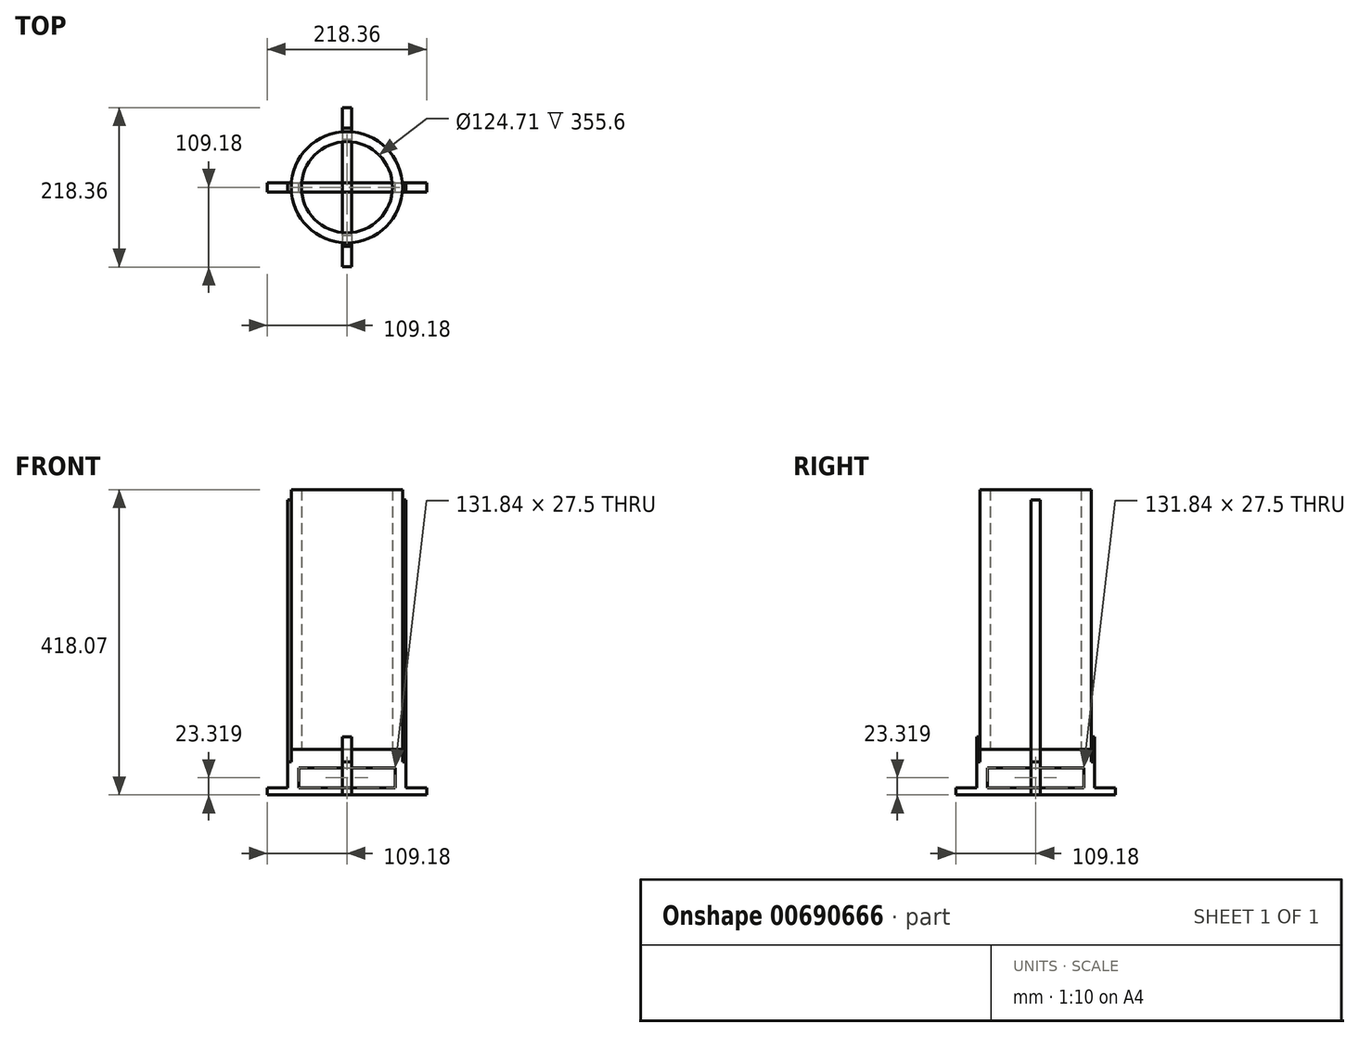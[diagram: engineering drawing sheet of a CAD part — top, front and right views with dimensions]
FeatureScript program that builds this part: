
annotation { "Feature Type Name" : "Feature", "Feature Type Description" : "" }
export const myFeature = defineFeature(function(context is Context, id is Id, definition is map)
    precondition{}
    {
        {
            var Q0;
            Q0=qCreatedBy(makeId("Top.planeOp"),FACE);
            var sketch = newSketch(context, id + "F0", { "sketchPlane" : qUnion([Q0])});
            skCircle(sketch, "E0", {"center": v(0, 0) * mm, "radius": 76.2 * mm});
            skCircle(sketch, "E1.0", {"center": v(0, 0) * mm, "radius": 62.36 * mm});
            skSolve(sketch);
        }
        {
            var Q0;
            Q0 = qSketchRegion(id + "F0", true);
            extrude(context, id + "F1", {"entities" : qUnion([Q0]), "depth" : 355.6 * mm, "offsetDistance" : 25.4 * mm});
        }
        {
            var Q0;
            Q0=qCreatedBy(makeId("Front.planeOp"),FACE);
            var sketch = newSketch(context, id + "F2", { "sketchPlane" : qUnion([Q0])});
            skLineSegment(sketch, "E2", {"start": v(0, 0) * mm, "end": v(76.2, 0) * mm});
            skLineSegment(sketch, "E3", {"start": v(65.92, -52.9) * mm, "end": v(65.92, -25.4) * mm});
            skLineSegment(sketch, "E4", {"start": v(65.92, -25.4) * mm, "end": v(0, -25.4) * mm});
            skLineSegment(sketch, "E5", {"start": v(76.2, 0) * mm, "end": v(76.2, -16.95) * mm});
            skLineSegment(sketch, "E6", {"start": v(76.2, -16.95) * mm, "end": v(80.84, -16.95) * mm});
            skLineSegment(sketch, "E7", {"start": v(80.84, -16.95) * mm, "end": v(80.84, -52.9) * mm});
            skLineSegment(sketch, "E8", {"start": v(0, 0) * mm, "end": v(0, -25.4) * mm});
            skLineSegment(sketch, "E9", {"start": v(80.84, -52.9) * mm, "end": v(65.92, -52.9) * mm});
            skLineSegment(sketch, "E10.bottom", {"start": v(0, -52.9) * mm, "end": v(0, -52.9) * mm});
            skLineSegment(sketch, "E10.left", {"start": v(0, -52.9) * mm, "end": v(0, -62.47) * mm});
            skLineSegment(sketch, "E10.right", {"start": v(0, -52.9) * mm, "end": v(0, -62.47) * mm});
            skLineSegment(sketch, "E11.bottom", {"start": v(0, -52.9) * mm, "end": v(109.18, -52.9) * mm});
            skLineSegment(sketch, "E11.top", {"start": v(0, -62.47) * mm, "end": v(109.18, -62.47) * mm});
            skLineSegment(sketch, "E11.right", {"start": v(109.18, -52.9) * mm, "end": v(109.18, -62.47) * mm});
            skLineSegment(sketch, "E12.MirrorCS", {"start": v(-76.2, -16.95) * mm, "end": v(-80.84, -16.95) * mm});
            skLineSegment(sketch, "E13.MirrorCS", {"start": v(-76.2, 0) * mm, "end": v(-76.2, -16.95) * mm});
            skLineSegment(sketch, "E14.MirrorCS", {"start": v(-80.84, -52.9) * mm, "end": v(-65.92, -52.9) * mm});
            skLineSegment(sketch, "E15.MirrorCS", {"start": v(-109.18, -52.9) * mm, "end": v(-109.18, -62.47) * mm});
            skLineSegment(sketch, "E16.MirrorCS", {"start": v(-65.92, -25.4) * mm, "end": v(0, -25.4) * mm});
            skLineSegment(sketch, "E17.MirrorCS", {"start": v(0, -52.9) * mm, "end": v(-109.18, -52.9) * mm});
            skLineSegment(sketch, "E18.MirrorCS", {"start": v(0, -62.47) * mm, "end": v(-109.18, -62.47) * mm});
            skLineSegment(sketch, "E19.MirrorCS", {"start": v(-65.92, -52.9) * mm, "end": v(-65.92, -25.4) * mm});
            skLineSegment(sketch, "E20.MirrorCS", {"start": v(0, 0) * mm, "end": v(-76.2, 0) * mm});
            skLineSegment(sketch, "E21.MirrorCS", {"start": v(-80.84, -16.95) * mm, "end": v(-80.84, -52.9) * mm});
            skSolve(sketch);
        }
        {
            var Q0;
            Q0 = qSketchRegion(id + "F2", true);
            extrude(context, id + "F3", {"entities" : qUnion([Q0]), "endBound" : BoundingType.SYMMETRIC, "depth" : 12.7 * mm, "offsetDistance" : 25.4 * mm});
        }
        {
            var Q0;
            Q0=makeQuery(id+"F3.opExtrude","SWEPT_BODY",BODY,{"disambiguationData":[OSD([sQuery(id+"F2.wireOp",EDGE,"E2"),sQuery(id+"F2.wireOp",EDGE,"E3"),sQuery(id+"F2.wireOp",EDGE,"E4"),sQuery(id+"F2.wireOp",EDGE,"E5"),sQuery(id+"F2.wireOp",EDGE,"E6"),sQuery(id+"F2.wireOp",EDGE,"E7"),sQuery(id+"F2.wireOp",EDGE,"yYa1QQtk-rfeQ-uA0k-yN95-LENgFDuBBmhA"),sQuery(id+"F2.wireOp",EDGE,"RaL1Y38n-DL0R-HpUy-0Yu0-hKOuieMtGCDP"),sQuery(id+"F2.wireOp",EDGE,"KzeCX9vK-PA9l-fBDc-L8z4-hnWVkcK37siH"),sQuery(id+"F2.wireOp",EDGE,"7a3115bd-42c9-43fa-886f-b7d7f014f3800.MirrorCS"),sQuery(id+"F2.wireOp",EDGE,"93714e8b-1b55-43fa-9f0a-1818bfe9d4330.MirrorCS"),sQuery(id+"F2.wireOp",EDGE,"f685ec73-5cd7-40c9-a0cc-09a82770efb00.MirrorCS"),sQuery(id+"F2.wireOp",EDGE,"605de593-ab4b-4a38-8b95-8d2e6ad95e7e0.MirrorCS"),sQuery(id+"F2.wireOp",EDGE,"bd68596d-ea5b-43b6-8ec0-eaa4091035650.MirrorCS"),sQuery(id+"F2.wireOp",EDGE,"6dadb6d6-938b-41b2-89eb-21b29489f2620.MirrorCS"),sQuery(id+"F2.wireOp",EDGE,"35a6b2d6-89f1-42be-bee9-e52b24f0a85c0.MirrorCS"),sQuery(id+"F2.wireOp",EDGE,"99d46e2b-beb4-45a8-a67b-b38dd53197940.MirrorCS"),sQuery(id+"F2.wireOp",EDGE,"687b68df-4fec-4741-9a90-ace4315f9af80.MirrorCS")])]});
            transform(context, id + "F4", {"entities" : qUnion([Q0]), "transformType" : TransformType.COPY});
        }
        {
            var Q0;
            Q0=makeQuery(id+"F3.opExtrude","SWEPT_BODY",BODY,{"disambiguationData":[OSD([sQuery(id+"F2.wireOp",EDGE,"E2"),sQuery(id+"F2.wireOp",EDGE,"E3"),sQuery(id+"F2.wireOp",EDGE,"E4"),sQuery(id+"F2.wireOp",EDGE,"E5"),sQuery(id+"F2.wireOp",EDGE,"E6"),sQuery(id+"F2.wireOp",EDGE,"E7"),sQuery(id+"F2.wireOp",EDGE,"yYa1QQtk-rfeQ-uA0k-yN95-LENgFDuBBmhA"),sQuery(id+"F2.wireOp",EDGE,"RaL1Y38n-DL0R-HpUy-0Yu0-hKOuieMtGCDP"),sQuery(id+"F2.wireOp",EDGE,"KzeCX9vK-PA9l-fBDc-L8z4-hnWVkcK37siH"),sQuery(id+"F2.wireOp",EDGE,"7a3115bd-42c9-43fa-886f-b7d7f014f3800.MirrorCS"),sQuery(id+"F2.wireOp",EDGE,"93714e8b-1b55-43fa-9f0a-1818bfe9d4330.MirrorCS"),sQuery(id+"F2.wireOp",EDGE,"f685ec73-5cd7-40c9-a0cc-09a82770efb00.MirrorCS"),sQuery(id+"F2.wireOp",EDGE,"605de593-ab4b-4a38-8b95-8d2e6ad95e7e0.MirrorCS"),sQuery(id+"F2.wireOp",EDGE,"bd68596d-ea5b-43b6-8ec0-eaa4091035650.MirrorCS"),sQuery(id+"F2.wireOp",EDGE,"6dadb6d6-938b-41b2-89eb-21b29489f2620.MirrorCS"),sQuery(id+"F2.wireOp",EDGE,"35a6b2d6-89f1-42be-bee9-e52b24f0a85c0.MirrorCS"),sQuery(id+"F2.wireOp",EDGE,"99d46e2b-beb4-45a8-a67b-b38dd53197940.MirrorCS"),sQuery(id+"F2.wireOp",EDGE,"687b68df-4fec-4741-9a90-ace4315f9af80.MirrorCS")])]});
            var Q1;
            Q1=sQuery(id+"F2.wireOp",EDGE,"E8");
            transform(context, id + "F5", {"entities" : qUnion([Q0]), "transformType" : TransformType.ROTATION, "transformAxis" : qUnion([Q1]), "angle" : 90 * degree, "makeCopy" : false});
        }
        {
            var Q0;
            Q0=makeQuery(id+"F4.opPattern","COPY",FACE,{"derivedFrom":makeQuery(id+"F3.opExtrude","CAP_FACE",FACE,{"disambiguationData":[OSD([sQuery(id+"F2.wireOp",EDGE,"E2"),sQuery(id+"F2.wireOp",EDGE,"E3"),sQuery(id+"F2.wireOp",EDGE,"E4"),sQuery(id+"F2.wireOp",EDGE,"E5"),sQuery(id+"F2.wireOp",EDGE,"E6"),sQuery(id+"F2.wireOp",EDGE,"E7"),sQuery(id+"F2.wireOp",EDGE,"E11.bottom"),sQuery(id+"F2.wireOp",EDGE,"E11.top"),sQuery(id+"F2.wireOp",EDGE,"E11.right"),sQuery(id+"F2.wireOp",EDGE,"6d3937cc-c99b-4de3-b3db-85ad403e89ce3.MirrorCS"),sQuery(id+"F2.wireOp",EDGE,"E15.MirrorCS"),sQuery(id+"F2.wireOp",EDGE,"6d3937cc-c99b-4de3-b3db-85ad403e89ce8.MirrorCS"),sQuery(id+"F2.wireOp",EDGE,"E16.MirrorCS"),sQuery(id+"F2.wireOp",EDGE,"E17.MirrorCS"),sQuery(id+"F2.wireOp",EDGE,"E18.MirrorCS"),sQuery(id+"F2.wireOp",EDGE,"E19.MirrorCS"),sQuery(id+"F2.wireOp",EDGE,"E20.MirrorCS"),sQuery(id+"F2.wireOp",EDGE,"6d3937cc-c99b-4de3-b3db-85ad403e89ce15.MirrorCS"),sQuery(id+"F2.wireOp",EDGE,"E21.MirrorCS")])],"isStart":false}),"instanceName":"1"});
            var sketch = newSketch(context, id + "F6", { "sketchPlane" : qUnion([Q0])});
            skLineSegment(sketch, "E22.bottom", {"start": v(76.2, -16.95) * mm, "end": v(80.84, -16.95) * mm});
            skLineSegment(sketch, "E22.top", {"start": v(76.2, 341.82) * mm, "end": v(80.84, 341.82) * mm});
            skLineSegment(sketch, "E22.left", {"start": v(76.2, -16.95) * mm, "end": v(76.2, 341.82) * mm});
            skLineSegment(sketch, "E22.right", {"start": v(80.84, -16.95) * mm, "end": v(80.84, 341.82) * mm});
            skSolve(sketch);
        }
        {
            var Q0;
            {var subQ3=sQuery(id+"F6.wireOp",EDGE,"E22.bottom");Q0=makeQuery(id+"F6.imprint","IMPRINT",FACE,{"disambiguationData":[TD([[makeQuery(id+"F6.imprint","IMPRINT",EDGE,{"derivedFrom":subQ3}),1.0]])]});}
            extrude(context, id + "F7", {"entities" : qUnion([Q0]), "oppositeDirection" : true, "depth" : 12.7 * mm, "offsetDistance" : 25.4 * mm});
        }
        {
            var Q0;
            Q0=makeQuery(id+"F7.opExtrude","SWEPT_BODY",BODY,{"disambiguationData":[OSD([sQuery(id+"F6.wireOp",EDGE,"E22.bottom"),sQuery(id+"F6.wireOp",EDGE,"E22.top"),sQuery(id+"F6.wireOp",EDGE,"E22.left"),sQuery(id+"F6.wireOp",EDGE,"E22.right")])]});
            var Q1;
            Q1=sQuery(id+"F2.wireOp",EDGE,"E8");
            circularPattern(context, id + "F8", {"entities" : qUnion([Q0]), "axis" : qUnion([Q1]), "angle" : 360 * degree, "instanceCount" : 2, "equalSpace" : true});
        }
        {
            var Q0;
            Q0=makeQuery(id+"F3.opExtrude","CAP_FACE",FACE,{"disambiguationData":[OSD([sQuery(id+"F2.wireOp",EDGE,"E2"),sQuery(id+"F2.wireOp",EDGE,"E3"),sQuery(id+"F2.wireOp",EDGE,"E4"),sQuery(id+"F2.wireOp",EDGE,"E5"),sQuery(id+"F2.wireOp",EDGE,"E6"),sQuery(id+"F2.wireOp",EDGE,"E7"),sQuery(id+"F2.wireOp",EDGE,"E11.bottom"),sQuery(id+"F2.wireOp",EDGE,"E11.top"),sQuery(id+"F2.wireOp",EDGE,"E11.right"),sQuery(id+"F2.wireOp",EDGE,"E12.MirrorCS"),sQuery(id+"F2.wireOp",EDGE,"E13.MirrorCS"),sQuery(id+"F2.wireOp",EDGE,"E15.MirrorCS"),sQuery(id+"F2.wireOp",EDGE,"E16.MirrorCS"),sQuery(id+"F2.wireOp",EDGE,"E17.MirrorCS"),sQuery(id+"F2.wireOp",EDGE,"E18.MirrorCS"),sQuery(id+"F2.wireOp",EDGE,"E19.MirrorCS"),sQuery(id+"F2.wireOp",EDGE,"E20.MirrorCS"),sQuery(id+"F2.wireOp",EDGE,"E21.MirrorCS")])],"isStart":false});
            var sketch = newSketch(context, id + "F9", { "sketchPlane" : qUnion([Q0])});
            skLineSegment(sketch, "E23.bottom", {"start": v(76.2, -16.95) * mm, "end": v(80.84, -16.95) * mm});
            skLineSegment(sketch, "E23.top", {"start": v(76.2, 17.25) * mm, "end": v(80.84, 17.25) * mm});
            skLineSegment(sketch, "E23.left", {"start": v(76.2, -16.95) * mm, "end": v(76.2, 17.25) * mm});
            skLineSegment(sketch, "E23.right", {"start": v(80.84, -16.95) * mm, "end": v(80.84, 17.25) * mm});
            skSolve(sketch);
        }
        {
            var Q0;
            Q0 = qSketchRegion(id + "F9", true);
            extrude(context, id + "F10", {"entities" : qUnion([Q0]), "oppositeDirection" : true, "depth" : 12.7 * mm, "offsetDistance" : 25.4 * mm});
        }
        {
            var Q0;
            Q0=makeQuery(id+"F10.opExtrude","SWEPT_BODY",BODY,{"disambiguationData":[OSD([sQuery(id+"F9.wireOp",EDGE,"E23.bottom"),sQuery(id+"F9.wireOp",EDGE,"E23.top"),sQuery(id+"F9.wireOp",EDGE,"E23.left"),sQuery(id+"F9.wireOp",EDGE,"E23.right")])]});
            var Q1;
            Q1=sQuery(id+"F2.wireOp",EDGE,"E8");
            circularPattern(context, id + "F11", {"entities" : qUnion([Q0]), "axis" : qUnion([Q1]), "angle" : 360 * degree, "instanceCount" : 2, "equalSpace" : true});
        }
    });
